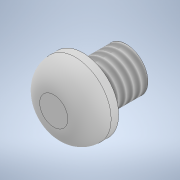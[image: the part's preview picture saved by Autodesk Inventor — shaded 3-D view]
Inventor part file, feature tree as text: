
AUTODESK INVENTOR PART (.ipt)
format: ipt  version: 2021 (Build 250183000, 183)  size: 130,560 bytes
history: native  units: mm
features: extrude x2, sketch x2, fillet x1, thread x1
ambient origin geometry x8: Origin, YZ Plane, XZ Plane, XY Plane, X Axis, Y Axis, Z Axis, Center Point
bodies: Solid1 (feature_tree)
feature tree (6):
  extrude  "Extrusion1"  Depth=2.7mm TaperAngle=0.0deg
  fillet  "Fillet1"  Radius=2.0mm
  extrude  "Extrusion2"  Depth=4.0mm TaperAngle=0.0deg
  thread  "Thread1"  [1 undecoded]
  sketch  "Sketch1"  dims[d0=6.6mm d1=2.7mm d2=0.0mm d3=2.0mm]
  sketch  "Sketch2"  dims[d4=4.0mm d5=4.0mm d6=0.0mm d7=5.0mm d8=0.0mm]
note: 1 required parameter value undecoded (feature->parameter linkage not recoverable at this tier; creation-order binding heuristic only, values carry confidence <= 0.55)
